# Revit family: Sanitary_Sanitary-Accessories_hansgrohe_41741XXX-AddStoris-Corner-basket_
name_source: partatom
category: Furniture
revit_build: Autodesk Revit 2015 (Build: 20140903_1530(x64)
units: mm (PartAtom-declared; Revit-internal decimal feet)

## types (6) — shared parameters
BIMobject category = Sanitary Accessories
BIMobject category code = sanitary-accessories1
BIMobject main category = Sanitary
BIMobject main category code = sanitary
Brand url = http://www.hansgrohe-int.com
Default Elevation = 1219.2 mm  [stored 4 ft]
Design country = Germany
Edition number = 1
GTIN code = https://4059625296868
IFC Classification = Sanitary Terminal
Installation instructions = https://www.hansgrohe.com
Manufacturer country = Germany
Manufacturer name = hansgrohe
Material main = Metal
Product Guid = 1d0b29e6-e3e2-4c1a-a047-8c97bf657bf6
Product SKU = 41741XXX
Product data url = https://bimobject.com
Product family = AddStoris
Product group = Soap dishes
Product name = 41741XXX AddStoris Corner basket
Product url = https://www.hansgrohe.com
QR code = http://bimobject.com
Technical description = https://www.hansgrohe.com

## type names (no varying parameters)
- 990 Polished Gold Optic
- 700 Matt White
- 670 Matte Black
- 340 Brushed Black Chrome
- 140 Brushed Bronze
- 000 Chrome

note: [stored X ft] marks values corroborated as IEEE doubles in the binary element streams (Revit-internal decimal feet)

## geometry (parser evidence)
native form markers: Sweep x2
no freeform markers — native parametric forms only
